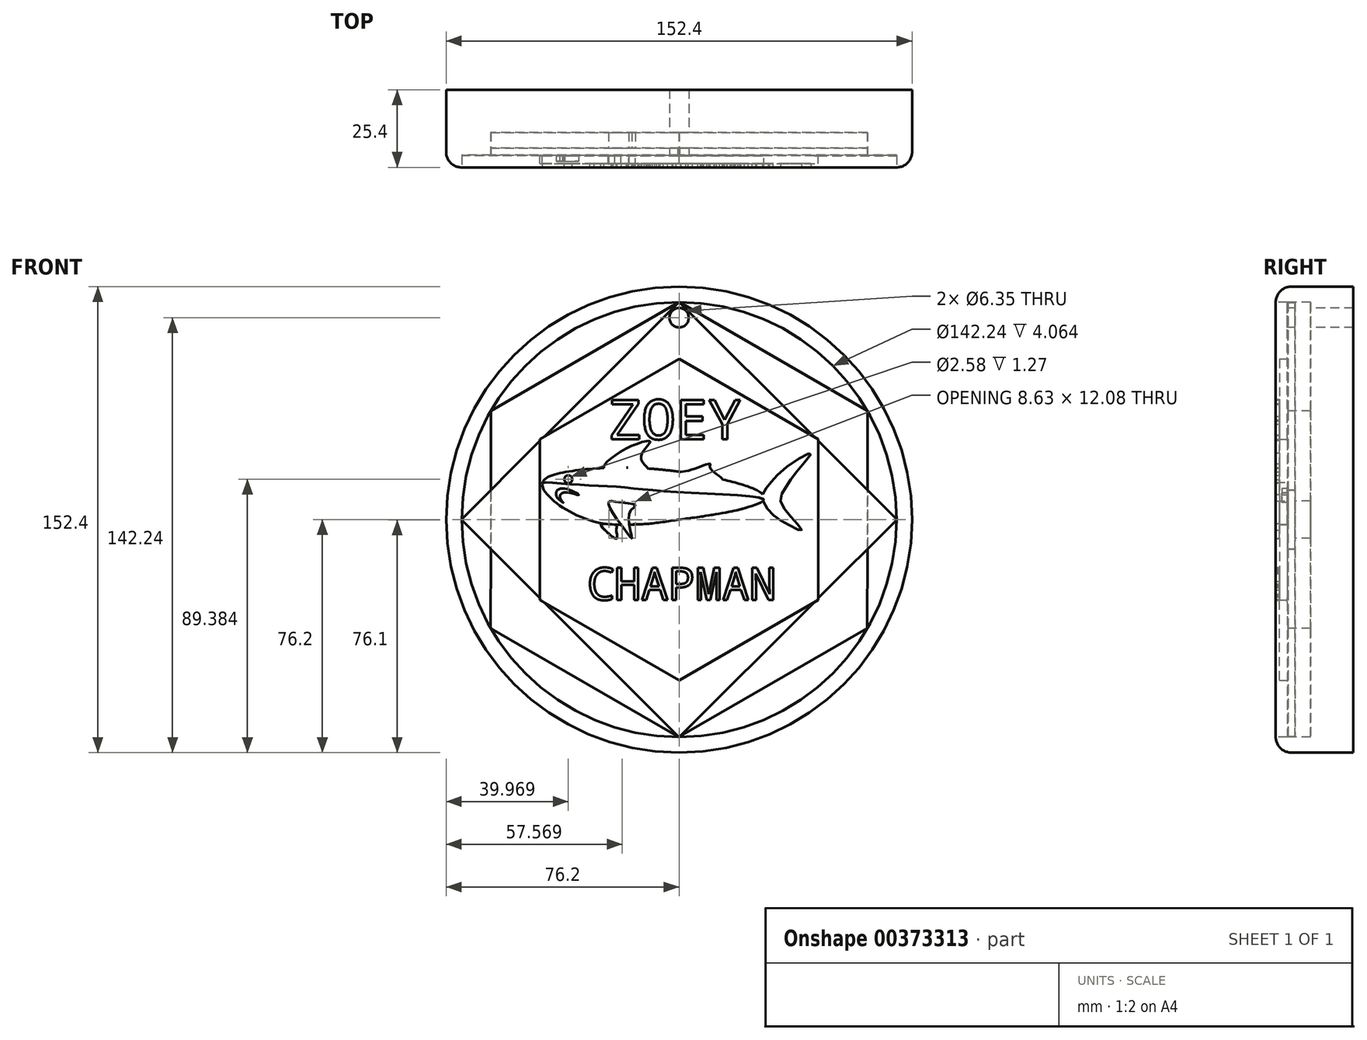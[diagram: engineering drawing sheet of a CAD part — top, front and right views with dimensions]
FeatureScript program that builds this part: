
annotation { "Feature Type Name" : "Feature", "Feature Type Description" : "" }
export const myFeature = defineFeature(function(context is Context, id is Id, definition is map)
    precondition{}
    {
        {
            var Q0;
            Q0=qCreatedBy(makeId("Front.planeOp"),FACE);
            var sketch = newSketch(context, id + "F0", { "sketchPlane" : qUnion([Q0])});
            skCircle(sketch, "E0", {"center": v(0, 0) * mm, "radius": 76.2 * mm});
            skSolve(sketch);
        }
        {
            var Q0;
            Q0=makeQuery(id+"F0.imprint","IMPRINT",FACE,{"disambiguationData":[TD([[makeQuery(id+"F0.imprint","IMPRINT",EDGE,{"derivedFrom":sQuery(id+"F0.wireOp",EDGE,"E0")}),1.0]])]});
            extrude(context, id + "F1", {"entities" : qUnion([Q0]), "depth" : 25.4 * mm, "symmetric" : true});
        }
        {
            var Q0;
            Q0=makeQuery(id+"F1.opExtrude","CAP_FACE",FACE,{"disambiguationData":[OSD([sQuery(id+"F0.wireOp",EDGE,"E0")])],"isStart":false});
            fillet(context, id + "F2", {"entities" : qUnion([Q0]), "radius" : 5.08 * mm, "tangentPropagation" : true, "allowEdgeOverflow" : false});
        }
        {
            var Q0;
            Q0=makeQuery(id+"F1.opExtrude","CAP_FACE",FACE,{"disambiguationData":[OSD([sQuery(id+"F0.wireOp",EDGE,"E0")])],"isStart":false});
            extrude(context, id + "F3", {"entities" : qUnion([Q0]), "operationType" : NewBodyOperationType.REMOVE, "oppositeDirection" : true, "depth" : 6.35 * mm});
        }
        {
            var Q0;
            Q0=makeQuery(id+"F3.boolean.opBoolean","COPY",FACE,{"derivedFrom":makeQuery(id+"F3.opExtrude","CAP_FACE",FACE,{"disambiguationData":[OSD([sQuery(id+"F0.wireOp",EDGE,"E0")])],"isStart":false})});
            var sketch = newSketch(context, id + "F4", { "sketchPlane" : qUnion([Q0])});
            skCircle(sketch, "E1.cCircle", {"center": v(0, 0) * mm, "radius": 71.12 * mm, "construction": true});
            skLineSegment(sketch, "E1.0", {"start": v(61.56, -35.6) * mm, "end": v(-0.06, -71.12) * mm});
            skLineSegment(sketch, "E1.1", {"start": v(-0.06, -71.12) * mm, "end": v(-61.62, -35.51) * mm});
            skLineSegment(sketch, "E1.2", {"start": v(-61.62, -35.51) * mm, "end": v(-61.56, 35.6) * mm});
            skLineSegment(sketch, "E1.3", {"start": v(-61.56, 35.6) * mm, "end": v(0.06, 71.12) * mm});
            skLineSegment(sketch, "E1.4", {"start": v(0.06, 71.12) * mm, "end": v(61.62, 35.51) * mm});
            skLineSegment(sketch, "E1.5", {"start": v(61.62, 35.51) * mm, "end": v(61.56, -35.6) * mm});
            skSolve(sketch);
        }
        {
            var Q0;
            {var subQ0=sQuery(id+"F4.wireOp",EDGE,"E1.3");Q0=makeQuery(id+"F4.imprint","IMPRINT",FACE,{"disambiguationData":[TD([[makeQuery(id+"F4.imprint","IMPRINT",EDGE,{"derivedFrom":subQ0}),1.0]])]});}
            var sketch = newSketch(context, id + "F5", { "sketchPlane" : qUnion([Q0])});
            skCircle(sketch, "E2.cCircle", {"center": v(0, 0) * mm, "radius": 71.2 * mm, "construction": true});
            skLineSegment(sketch, "E2.0", {"start": v(71.2, 0) * mm, "end": v(0, -71.2) * mm});
            skLineSegment(sketch, "E2.1", {"start": v(0, -71.2) * mm, "end": v(-71.2, 0) * mm});
            skLineSegment(sketch, "E2.2", {"start": v(-71.2, 0) * mm, "end": v(0, 71.2) * mm});
            skLineSegment(sketch, "E2.3", {"start": v(0, 71.2) * mm, "end": v(71.2, 0) * mm});
            skSolve(sketch);
        }
        {
            var Q0;
            Q0=makeQuery(id+"F4.imprint","IMPRINT",FACE,{"disambiguationData":[TD([[makeQuery(id+"F4.imprint","IMPRINT",EDGE,{"derivedFrom":sQuery(id+"F4.wireOp",EDGE,"E1.0")}),-1.0]])]});
            extrude(context, id + "F6", {"entities" : qUnion([Q0]), "operationType" : NewBodyOperationType.REMOVE, "oppositeDirection" : true, "depth" : 5.08 * mm});
        }
        {
            var Q0;
            {var subQ0=sQuery(id+"F5.wireOp",EDGE,"E2.2");var subQ1=sQuery(id+"F4.wireOp",EDGE,"E1.3");var subQ2=makeQuery(id+"F4.imprint","IMPRINT",EDGE,{"derivedFrom":subQ1});var subQ3=makeQuery(id+"F5.imprint","INTERSECT",VERTEX,{"derivedFrom":[subQ2,subQ0]});Q0=makeQuery(id+"F5.imprint","IMPRINT",FACE,{"disambiguationData":[TD([[makeQuery(id+"F5.imprint","IMPRINT",EDGE,{"disambiguationData":[TD([[subQ3,-1.0]])],"derivedFrom":subQ0}),1.0]])]});}
            var Q1;
            {var subQ0=sQuery(id+"F0.wireOp",EDGE,"E0");var subQ1=makeQuery(id+"F3.boolean.opBoolean","COPY",FACE,{"derivedFrom":makeQuery(id+"F3.opExtrude","CAP_FACE",FACE,{"disambiguationData":[OSD([subQ0])],"isStart":false})});Q1=makeQuery(id+"F6.boolean.opBoolean","SPLIT",FACE,{"disambiguationData":[TD([makeQuery(id+"F3.boolean.opBoolean","COPY",FACE,{"derivedFrom":makeQuery(id+"F3.opExtrude","SWEPT_FACE",FACE,{"disambiguationData":[OSD([subQ0])]})}),subQ1,makeQuery(id+"F6.opExtrude","SWEPT_FACE",FACE,{"disambiguationData":[OSD([sQuery(id+"F4.wireOp",EDGE,"E1.1")])]}),makeQuery(id+"F6.opExtrude","SWEPT_FACE",FACE,{"disambiguationData":[OSD([sQuery(id+"F4.wireOp",EDGE,"E1.2")])]}),makeQuery(id+"F6.opExtrude","SWEPT_FACE",FACE,{"disambiguationData":[OSD([sQuery(id+"F4.wireOp",EDGE,"E1.3")])]})])],"derivedFrom":subQ1});}
            var Q2;
            {var subQ0=sQuery(id+"F0.wireOp",EDGE,"E0");var subQ1=makeQuery(id+"F3.boolean.opBoolean","COPY",FACE,{"derivedFrom":makeQuery(id+"F3.opExtrude","CAP_FACE",FACE,{"disambiguationData":[OSD([subQ0])],"isStart":false})});Q2=makeQuery(id+"F6.boolean.opBoolean","SPLIT",FACE,{"disambiguationData":[TD([makeQuery(id+"F3.boolean.opBoolean","COPY",FACE,{"derivedFrom":makeQuery(id+"F3.opExtrude","SWEPT_FACE",FACE,{"disambiguationData":[OSD([subQ0])]})}),subQ1,makeQuery(id+"F6.opExtrude","SWEPT_FACE",FACE,{"disambiguationData":[OSD([sQuery(id+"F4.wireOp",EDGE,"E1.0")])]}),makeQuery(id+"F6.opExtrude","SWEPT_FACE",FACE,{"disambiguationData":[OSD([sQuery(id+"F4.wireOp",EDGE,"E1.1")])]}),makeQuery(id+"F6.opExtrude","SWEPT_FACE",FACE,{"disambiguationData":[OSD([sQuery(id+"F4.wireOp",EDGE,"E1.2")])]})])],"derivedFrom":subQ1});}
            var Q3;
            {var subQ0=sQuery(id+"F0.wireOp",EDGE,"E0");var subQ1=makeQuery(id+"F3.boolean.opBoolean","COPY",FACE,{"derivedFrom":makeQuery(id+"F3.opExtrude","CAP_FACE",FACE,{"disambiguationData":[OSD([subQ0])],"isStart":false})});Q3=makeQuery(id+"F6.boolean.opBoolean","SPLIT",FACE,{"disambiguationData":[TD([makeQuery(id+"F3.boolean.opBoolean","COPY",FACE,{"derivedFrom":makeQuery(id+"F3.opExtrude","SWEPT_FACE",FACE,{"disambiguationData":[OSD([subQ0])]})}),subQ1,makeQuery(id+"F6.opExtrude","SWEPT_FACE",FACE,{"disambiguationData":[OSD([sQuery(id+"F4.wireOp",EDGE,"E1.0")])]}),makeQuery(id+"F6.opExtrude","SWEPT_FACE",FACE,{"disambiguationData":[OSD([sQuery(id+"F4.wireOp",EDGE,"E1.1")])]}),makeQuery(id+"F6.opExtrude","SWEPT_FACE",FACE,{"disambiguationData":[OSD([sQuery(id+"F4.wireOp",EDGE,"E1.5")])]})])],"derivedFrom":subQ1});}
            var Q4;
            {var subQ0=sQuery(id+"F0.wireOp",EDGE,"E0");var subQ1=makeQuery(id+"F3.boolean.opBoolean","COPY",FACE,{"derivedFrom":makeQuery(id+"F3.opExtrude","CAP_FACE",FACE,{"disambiguationData":[OSD([subQ0])],"isStart":false})});Q4=makeQuery(id+"F6.boolean.opBoolean","SPLIT",FACE,{"disambiguationData":[TD([makeQuery(id+"F3.boolean.opBoolean","COPY",FACE,{"derivedFrom":makeQuery(id+"F3.opExtrude","SWEPT_FACE",FACE,{"disambiguationData":[OSD([subQ0])]})}),subQ1,makeQuery(id+"F6.opExtrude","SWEPT_FACE",FACE,{"disambiguationData":[OSD([sQuery(id+"F4.wireOp",EDGE,"E1.0")])]}),makeQuery(id+"F6.opExtrude","SWEPT_FACE",FACE,{"disambiguationData":[OSD([sQuery(id+"F4.wireOp",EDGE,"E1.4")])]}),makeQuery(id+"F6.opExtrude","SWEPT_FACE",FACE,{"disambiguationData":[OSD([sQuery(id+"F4.wireOp",EDGE,"E1.5")])]})])],"derivedFrom":subQ1});}
            var Q5;
            {var subQ0=sQuery(id+"F0.wireOp",EDGE,"E0");var subQ1=makeQuery(id+"F3.boolean.opBoolean","COPY",FACE,{"derivedFrom":makeQuery(id+"F3.opExtrude","CAP_FACE",FACE,{"disambiguationData":[OSD([subQ0])],"isStart":false})});Q5=makeQuery(id+"F6.boolean.opBoolean","SPLIT",FACE,{"disambiguationData":[TD([makeQuery(id+"F3.boolean.opBoolean","COPY",FACE,{"derivedFrom":makeQuery(id+"F3.opExtrude","SWEPT_FACE",FACE,{"disambiguationData":[OSD([subQ0])]})}),subQ1,makeQuery(id+"F6.opExtrude","SWEPT_FACE",FACE,{"disambiguationData":[OSD([sQuery(id+"F4.wireOp",EDGE,"E1.3")])]}),makeQuery(id+"F6.opExtrude","SWEPT_FACE",FACE,{"disambiguationData":[OSD([sQuery(id+"F4.wireOp",EDGE,"E1.4")])]}),makeQuery(id+"F6.opExtrude","SWEPT_FACE",FACE,{"disambiguationData":[OSD([sQuery(id+"F4.wireOp",EDGE,"E1.5")])]})])],"derivedFrom":subQ1});}
            var Q6;
            Q6 = qSketchRegion(id + "FbXj7fASeFlP7Ip_1", true);
            extrude(context, id + "F7", {"entities" : qUnion([Q0, Q1, Q2, Q3, Q4, Q5, Q6]), "operationType" : NewBodyOperationType.ADD, "depth" : 2.3 * mm});
        }
        {
            var Q0;
            Q0=makeQuery(id+"F5.imprint","IMPRINT",FACE,{"disambiguationData":[TD([[makeQuery(id+"F5.imprint","IMPRINT",EDGE,{"derivedFrom":sQuery(id+"F5.wireOp",EDGE,"E2.0")}),-1.0]])]});
            var Q1;
            Q1 = qSketchRegion(id + "F5", true);
            extrude(context, id + "F8", {"entities" : qUnion([Q0, Q1]), "operationType" : NewBodyOperationType.ADD, "depth" : 2.54 * mm});
        }
        {
            var Q0;
            Q0=makeQuery(id+"F8.opExtrude","CAP_FACE",FACE,{"disambiguationData":[OSD([sQuery(id+"F5.wireOp",EDGE,"E2.0"),sQuery(id+"F5.wireOp",EDGE,"E2.1"),sQuery(id+"F5.wireOp",EDGE,"E2.2"),sQuery(id+"F5.wireOp",EDGE,"E2.3")])],"isStart":false});
            var sketch = newSketch(context, id + "F9", { "sketchPlane" : qUnion([Q0])});
            skFitSpline(sketch, "E3", {"points": [v(-44.67, 11.8) * mm, v(-34.47, 15.98) * mm, v(0, 15.67) * mm, v(27.72, 7.35) * mm, v(0, 0) * mm, v(-32.3, 0.9) * mm, v(-44.67, 11.8) * mm]});
            skFitSpline(sketch, "E4", {"points": [v(-24.65, 16.87) * mm, v(-18.77, 22.43) * mm, v(-9.46, 25.46) * mm, v(-12.52, 20.3) * mm, v(-10.18, 16.7) * mm, v(-17.23, 16.98) * mm, v(-24.65, 16.87) * mm]});
            skSolve(sketch);
        }
        {
            var Q0;
            {var subQ3=sQuery(id+"F5.wireOp",EDGE,"E2.0");Q0=makeQuery(id+"F9.imprint","IMPRINT",FACE,{"disambiguationData":[TD([[makeQuery(id+"F9.imprint","IMPRINT",EDGE,{"derivedFrom":makeQuery(id+"F8.opExtrude","CAP_EDGE",EDGE,{"disambiguationData":[OSD([subQ3])],"isStart":false})}),-1.0]])]});}
            var sketch = newSketch(context, id + "F10", { "sketchPlane" : qUnion([Q0])});
            skFitSpline(sketch, "E5", {"points": [v(0, 15.35) * mm, v(7.32, 14.15) * mm, v(14.27, 13.15) * mm, v(10.13, 16.95) * mm, v(10.13, 18.23) * mm, v(3.78, 16.22) * mm, v(0, 15.35) * mm]});
            skSolve(sketch);
        }
        {
            var Q0;
            {var subQ3=sQuery(id+"F5.wireOp",EDGE,"E2.0");Q0=makeQuery(id+"F9.imprint","IMPRINT",FACE,{"disambiguationData":[TD([[makeQuery(id+"F9.imprint","IMPRINT",EDGE,{"derivedFrom":makeQuery(id+"F8.opExtrude","CAP_EDGE",EDGE,{"disambiguationData":[OSD([subQ3])],"isStart":false})}),-1.0]])]});}
            var sketch = newSketch(context, id + "F11", { "sketchPlane" : qUnion([Q0])});
            skFitSpline(sketch, "E6", {"points": [v(-44.71, 11.9) * mm, v(-36.07, 11.62) * mm, v(-20.01, 10.69) * mm, v(0, 8.93) * mm, v(27.72, 6.54) * mm, v(24.88, 4.87) * mm, v(17.88, 2.86) * mm, v(5.06, 0.66) * mm, v(0, 0) * mm, v(-9.34, -1.3) * mm, v(-14.7, -1.58) * mm, v(-22.05, -1.62) * mm, v(-29.89, 0) * mm, v(-35.6, 2.47) * mm, v(-39.77, 5.16) * mm, v(-42.53, 7.6) * mm, v(-44.3, 9.87) * mm, v(-44.7, 11.23) * mm, v(-44.71, 11.9) * mm]});
            skPoint(sketch, "E7", {"position": v(-26.84, -0.86) * mm});
            skSolve(sketch);
        }
        {
            var Q0;
            Q0=qCreatedBy(makeId("Front.planeOp"),FACE);
            var sketch = newSketch(context, id + "F12", { "sketchPlane" : qUnion([Q0])});
            skFitSpline(sketch, "E8", {"points": [v(-22.95, 5.94) * mm, v(-22.14, 2.92) * mm, v(-17.31, -3.93) * mm, v(-15.5, -6.14) * mm, v(-16.3, -1.5) * mm, v(-15.7, 3.12) * mm, v(-14.3, 4.73) * mm, v(-19.93, 5.74) * mm, v(-22.95, 5.94) * mm]});
            skSolve(sketch);
        }
        {
            var Q0;
            {var subQ0=sQuery(id+"F9.wireOp",EDGE,"E4");var subQ1=sQuery(id+"F9.wireOp",EDGE,"E3");var subQ7=makeQuery(id+"F9.imprint","INTERSECT",VERTEX,{"disambiguationData":[OD(0.0)],"derivedFrom":[subQ1,subQ0]});Q0=makeQuery(id+"F9.imprint","IMPRINT",FACE,{"disambiguationData":[TD([[makeQuery(id+"F9.imprint","IMPRINT",EDGE,{"disambiguationData":[TD([[subQ7,-1.0]])],"derivedFrom":subQ1}),-1.0]])]});}
            var sketch = newSketch(context, id + "F13", { "sketchPlane" : qUnion([Q0])});
            skFitSpline(sketch, "E9", {"points": [v(-25.56, -1.5) * mm, v(-23.35, -4.33) * mm, v(-20.33, -6.14) * mm, v(-20.53, -3.32) * mm, v(-20.53, -1.91) * mm, v(-23.15, -1.5) * mm, v(-25.56, -1.5) * mm]});
            skSolve(sketch);
        }
        {
            var Q0;
            {var subQ3=sQuery(id+"F5.wireOp",EDGE,"E2.0");Q0=makeQuery(id+"F9.imprint","IMPRINT",FACE,{"disambiguationData":[TD([[makeQuery(id+"F9.imprint","IMPRINT",EDGE,{"derivedFrom":makeQuery(id+"F8.opExtrude","CAP_EDGE",EDGE,{"disambiguationData":[OSD([subQ3])],"isStart":false})}),-1.0]])]});}
            var sketch = newSketch(context, id + "F14", { "sketchPlane" : qUnion([Q0])});
            skFitSpline(sketch, "E10", {"points": [v(27.17, 7.35) * mm, v(28.98, 10.97) * mm, v(34.42, 16.6) * mm, v(43.07, 21.64) * mm, v(39.05, 16.4) * mm, v(34.62, 10.16) * mm, v(33.21, 5.94) * mm, v(37.44, 0) * mm, v(40.06, -3.52) * mm, v(35.43, -1.5) * mm, v(30, 2.31) * mm, v(27.17, 7.35) * mm]});
            skSolve(sketch);
        }
        {
            var Q0;
            {var subQ3=sQuery(id+"F5.wireOp",EDGE,"E2.0");Q0=makeQuery(id+"F10.imprint","IMPRINT",FACE,{"disambiguationData":[TD([[makeQuery(id+"F10.imprint","IMPRINT",EDGE,{"derivedFrom":makeQuery(id+"F9.imprint","IMPRINT",EDGE,{"derivedFrom":makeQuery(id+"F8.opExtrude","CAP_EDGE",EDGE,{"disambiguationData":[OSD([subQ3])],"isStart":false})})}),-1.0]])]});}
            var sketch = newSketch(context, id + "F15", { "sketchPlane" : qUnion([Q0])});
            skText(sketch, "E11", { "text": "CHAPMAN", "fontName": "DroidSansMono.ttf"});
            const initialGuessF15  = {"E11": [-0.03007, -0.0263, 1, 0, 0.0106]};
            skSetInitialGuess(sketch, initialGuessF15);
            skSolve(sketch);
        }
        {
            var Q0;
            {var subQ7=sQuery(id+"F5.wireOp",EDGE,"E2.0");Q0=makeQuery(id+"F9.imprint","IMPRINT",FACE,{"disambiguationData":[TD([[makeQuery(id+"F9.imprint","IMPRINT",EDGE,{"derivedFrom":makeQuery(id+"F8.opExtrude","CAP_EDGE",EDGE,{"disambiguationData":[OSD([subQ7])],"isStart":false})}),-1.0]])]});}
            var sketch = newSketch(context, id + "F16", { "sketchPlane" : qUnion([Q0])});
            skCircle(sketch, "E12.cCircle", {"center": v(0, 0) * mm, "radius": 45.49 * mm, "construction": true});
            skLineSegment(sketch, "E12.0", {"start": v(45.49, 26.26) * mm, "end": v(45.49, -26.26) * mm});
            skLineSegment(sketch, "E12.1", {"start": v(45.49, -26.26) * mm, "end": v(0, -52.53) * mm});
            skLineSegment(sketch, "E12.2", {"start": v(0, -52.53) * mm, "end": v(-45.49, -26.26) * mm});
            skLineSegment(sketch, "E12.3", {"start": v(-45.49, -26.26) * mm, "end": v(-45.49, 26.26) * mm});
            skLineSegment(sketch, "E12.4", {"start": v(-45.49, 26.26) * mm, "end": v(0, 52.53) * mm});
            skLineSegment(sketch, "E12.5", {"start": v(0, 52.53) * mm, "end": v(45.49, 26.26) * mm});
            skPoint(sketch, "E12.0.midPoint", {"position": v(45.49, 0) * mm});
            skSolve(sketch);
        }
        {
            var Q0;
            Q0 = qSketchRegion(id + "F16", true);
            extrude(context, id + "F17", {"entities" : qUnion([Q0]), "operationType" : NewBodyOperationType.ADD, "depth" : 2.54 * mm});
        }
        {
            var Q0;
            Q0 = qSketchRegion(id + "F15", true);
            extrude(context, id + "F18", {"entities" : qUnion([Q0]), "operationType" : NewBodyOperationType.ADD, "depth" : 3.8 * mm});
        }
        {
            var Q0;
            {var subQ7=sQuery(id+"F5.wireOp",EDGE,"E2.0");Q0=makeQuery(id+"F9.imprint","IMPRINT",FACE,{"disambiguationData":[TD([[makeQuery(id+"F9.imprint","IMPRINT",EDGE,{"derivedFrom":makeQuery(id+"F8.opExtrude","CAP_EDGE",EDGE,{"disambiguationData":[OSD([subQ7])],"isStart":false})}),-1.0]])]});}
            var sketch = newSketch(context, id + "F19", { "sketchPlane" : qUnion([Q0])});
            skCircle(sketch, "E13", {"center": v(0, 66.04) * mm, "radius": 3.18 * mm});
            skSolve(sketch);
        }
        {
            var Q0;
            Q0=sQuery(id+"F19.wireOp",VERTEX,"E13.center");
            var Q1;
            Q1=makeQuery(id+"F1.opExtrude","SWEPT_BODY",BODY,{"disambiguationData":[OSD([sQuery(id+"F0.wireOp",EDGE,"E0")])]});
            hole(context, id + "F20", {"style" : HoleStyle.SIMPLE, "endStyle" : HoleEndStyle.THROUGH, "holeDiameter" : 6.35 * mm, "isTappedThrough" : true, "tappedDepth" : 12.7 * mm, "tapClearance" : 3, "locations" : qUnion([Q0]), "scope" : qUnion([Q1])});
        }
        {
            var Q0;
            Q0 = qSketchRegion(id + "F9", true);
            extrude(context, id + "F21", {"entities" : qUnion([Q0]), "operationType" : NewBodyOperationType.ADD, "depth" : 3.8 * mm});
        }
        {
            var Q0;
            Q0 = qSketchRegion(id + "F10", true);
            extrude(context, id + "F22", {"entities" : qUnion([Q0]), "operationType" : NewBodyOperationType.ADD, "depth" : 3.8 * mm});
        }
        {
            var Q0;
            Q0 = qSketchRegion(id + "F14", true);
            extrude(context, id + "F23", {"entities" : qUnion([Q0]), "operationType" : NewBodyOperationType.ADD, "depth" : 3.8 * mm});
        }
        {
            var Q0;
            Q0 = qSketchRegion(id + "F11", true);
            extrude(context, id + "F24", {"entities" : qUnion([Q0]), "operationType" : NewBodyOperationType.REMOVE, "depth" : 3.8 * mm});
        }
        {
            var Q0;
            Q0 = qSketchRegion(id + "F12", true);
            extrude(context, id + "F25", {"entities" : qUnion([Q0]), "operationType" : NewBodyOperationType.ADD, "depth" : 12.7 * mm});
        }
        {
            var Q0;
            Q0 = qSketchRegion(id + "F13", true);
            extrude(context, id + "F26", {"entities" : qUnion([Q0]), "operationType" : NewBodyOperationType.ADD, "depth" : 3.8 * mm});
        }
        {
            var Q0;
            {var subQ22=sQuery(id+"F16.wireOp",EDGE,"E12.0");var subQ23=makeQuery(id+"F17.opExtrude","SWEPT_FACE",FACE,{"disambiguationData":[OSD([subQ22])]});var subQ28=sQuery(id+"F16.wireOp",EDGE,"E12.5");var subQ35=sQuery(id+"F16.wireOp",EDGE,"E12.4");var subQ40=sQuery(id+"F16.wireOp",EDGE,"E12.3");var subQ46=sQuery(id+"F16.wireOp",EDGE,"E12.1");var subQ52=sQuery(id+"F16.wireOp",EDGE,"E12.2");Q0=makeQuery(id+"F21.boolean.opBoolean","SPLIT",FACE,{"disambiguationData":[TD([subQ23])],"derivedFrom":makeQuery(id+"F18.boolean.opBoolean","SPLIT",FACE,{"disambiguationData":[TD([subQ23])],"derivedFrom":makeQuery(id+"F17.opExtrude","CAP_FACE",FACE,{"disambiguationData":[OSD([subQ22,subQ46,subQ52,subQ40,subQ35,subQ28])],"isStart":false})})});}
            var sketch = newSketch(context, id + "F27", { "sketchPlane" : qUnion([Q0])});
            skCircle(sketch, "E14", {"center": v(-36.23, 13.18) * mm, "radius": 1.29 * mm});
            skSolve(sketch);
        }
        {
            var Q0;
            Q0 = qSketchRegion(id + "F27", true);
            extrude(context, id + "F28", {"entities" : qUnion([Q0]), "operationType" : NewBodyOperationType.REMOVE, "depth" : 1.52 * mm});
        }
        {
            var Q0;
            Q0=makeQuery(id+"F24.boolean.opBoolean","COPY",FACE,{"derivedFrom":makeQuery(id+"F24.opExtrude","CAP_FACE",FACE,{"disambiguationData":[OSD([sQuery(id+"F11.wireOp",EDGE,"E6")])],"isStart":true})});
            var sketch = newSketch(context, id + "F29", { "sketchPlane" : qUnion([Q0])});
            skFitSpline(sketch, "E15", {"points": [v(-39.57, 6.77) * mm, v(-40.23, 8.44) * mm, v(-39.7, 9.76) * mm, v(-37.6, 10.12) * mm, v(-34.6, 9.22) * mm, v(-32.81, 8.02) * mm, v(-34.13, 8.38) * mm, v(-36.58, 8.89) * mm, v(-38.26, 8.64) * mm, v(-38.97, 7.72) * mm, v(-38.5, 6.29) * mm, v(-37.9, 5.56) * mm, v(-39.57, 6.77) * mm]});
            skLineSegment(sketch, "E16", {"start": v(-37.9, 5.56) * mm, "end": v(-38.97, 6.5) * mm});
            skLineSegment(sketch, "E17", {"start": v(-38.97, 6.5) * mm, "end": v(-38.64, 6.5) * mm});
            skLineSegment(sketch, "E18", {"start": v(-38.64, 6.5) * mm, "end": v(-39.57, 7.31) * mm});
            skLineSegment(sketch, "E19", {"start": v(-39.57, 7.31) * mm, "end": v(-38.99, 7.45) * mm});
            skLineSegment(sketch, "E20", {"start": v(-38.99, 7.45) * mm, "end": v(-39.9, 8.43) * mm});
            skLineSegment(sketch, "E21", {"start": v(-39.9, 8.43) * mm, "end": v(-38.76, 8.22) * mm});
            skLineSegment(sketch, "E22", {"start": v(-38.76, 8.22) * mm, "end": v(-39.4, 9.35) * mm});
            skLineSegment(sketch, "E23", {"start": v(-39.4, 9.35) * mm, "end": v(-38.18, 8.68) * mm});
            skLineSegment(sketch, "E24", {"start": v(-38.18, 8.68) * mm, "end": v(-38.6, 9.7) * mm});
            skLineSegment(sketch, "E25", {"start": v(-38.6, 9.7) * mm, "end": v(-37.3, 8.89) * mm});
            skLineSegment(sketch, "E26", {"start": v(-37.3, 8.89) * mm, "end": v(-37.43, 9.74) * mm});
            skLineSegment(sketch, "E27", {"start": v(-37.43, 9.74) * mm, "end": v(-36.42, 8.87) * mm});
            skLineSegment(sketch, "E28", {"start": v(-36.42, 8.87) * mm, "end": v(-36.48, 9.63) * mm});
            skLineSegment(sketch, "E29", {"start": v(-36.48, 9.63) * mm, "end": v(-35.8, 8.8) * mm});
            skLineSegment(sketch, "E30", {"start": v(-35.8, 8.8) * mm, "end": v(-35.82, 9.44) * mm});
            skLineSegment(sketch, "E31", {"start": v(-35.82, 9.44) * mm, "end": v(-35.2, 8.67) * mm});
            skLineSegment(sketch, "E32", {"start": v(-35.2, 8.67) * mm, "end": v(-35.11, 9.22) * mm});
            skLineSegment(sketch, "E33", {"start": v(-35.11, 9.22) * mm, "end": v(-34.59, 8.51) * mm});
            skLineSegment(sketch, "E34", {"start": v(-34.59, 8.51) * mm, "end": v(-34.59, 8.9) * mm});
            skLineSegment(sketch, "E35", {"start": v(-34.59, 8.9) * mm, "end": v(-34.13, 8.38) * mm});
            skSolve(sketch);
        }
        {
            var Q0;
            Q0 = qSketchRegion(id + "F29", true);
            extrude(context, id + "F30", {"entities" : qUnion([Q0]), "operationType" : NewBodyOperationType.ADD, "depth" : 1.78 * mm});
        }
        {
            var Q0;
            {var subQ22=sQuery(id+"F16.wireOp",EDGE,"E12.0");var subQ23=makeQuery(id+"F17.opExtrude","SWEPT_FACE",FACE,{"disambiguationData":[OSD([subQ22])]});var subQ28=sQuery(id+"F16.wireOp",EDGE,"E12.5");var subQ35=sQuery(id+"F16.wireOp",EDGE,"E12.4");var subQ40=sQuery(id+"F16.wireOp",EDGE,"E12.3");var subQ46=sQuery(id+"F16.wireOp",EDGE,"E12.1");var subQ52=sQuery(id+"F16.wireOp",EDGE,"E12.2");Q0=makeQuery(id+"F21.boolean.opBoolean","SPLIT",FACE,{"disambiguationData":[TD([subQ23])],"derivedFrom":makeQuery(id+"F18.boolean.opBoolean","SPLIT",FACE,{"disambiguationData":[TD([subQ23])],"derivedFrom":makeQuery(id+"F17.opExtrude","CAP_FACE",FACE,{"disambiguationData":[OSD([subQ22,subQ46,subQ52,subQ40,subQ35,subQ28])],"isStart":false})})});}
            var sketch = newSketch(context, id + "F31", { "sketchPlane" : qUnion([Q0])});
            skText(sketch, "E36", { "text": "ZOEY\n", "fontName": "DroidSansMono.ttf"});
            skPoint(sketch, "E36.secondSnap0", {"position": v(22.74, 39.4) * mm});
            const initialGuessF31  = {"E36": [-0.02299, 0.02626, 1, 0, 0.013]};
            skSetInitialGuess(sketch, initialGuessF31);
            skSolve(sketch);
        }
        {
            var Q0;
            Q0 = qSketchRegion(id + "F31", true);
            extrude(context, id + "F32", {"entities" : qUnion([Q0]), "operationType" : NewBodyOperationType.ADD, "depth" : 1.27 * mm});
        }
    });
